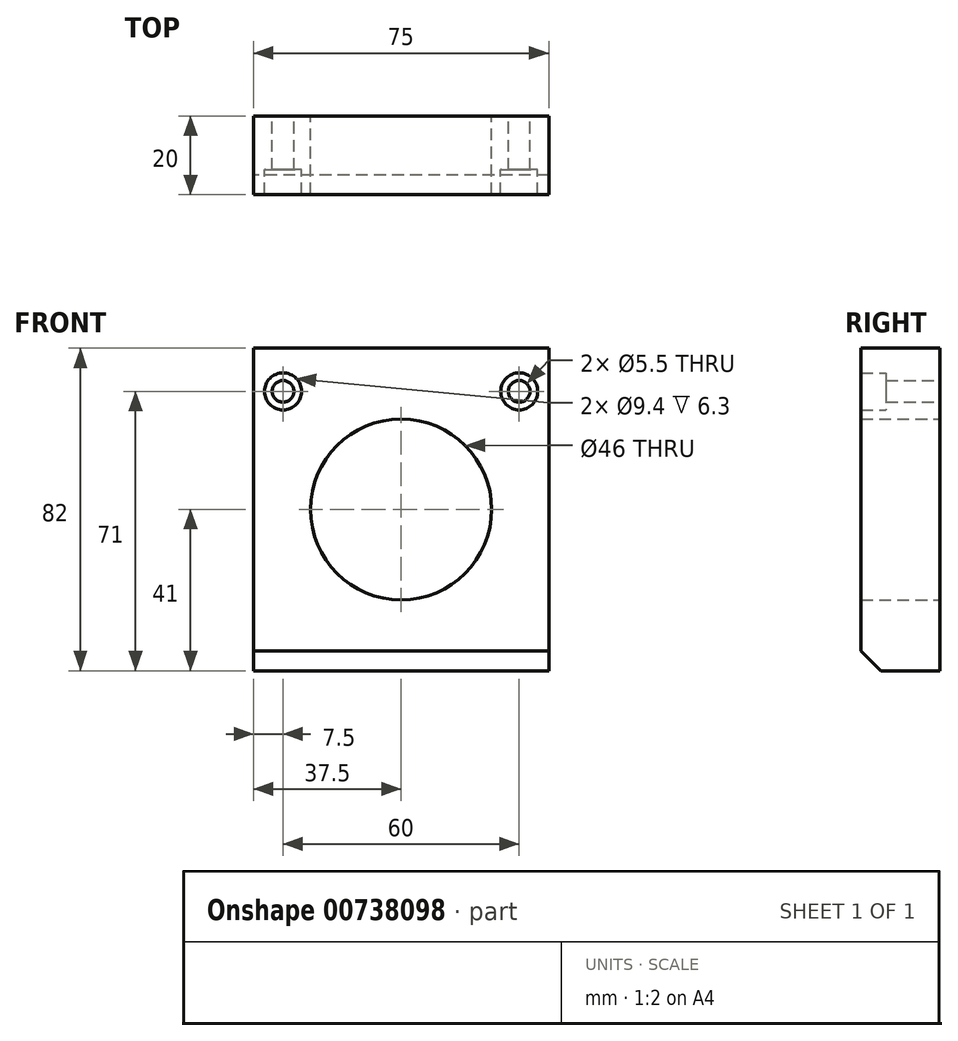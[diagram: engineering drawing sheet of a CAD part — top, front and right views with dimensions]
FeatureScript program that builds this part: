
annotation { "Feature Type Name" : "Feature", "Feature Type Description" : "" }
export const myFeature = defineFeature(function(context is Context, id is Id, definition is map)
    precondition{}
    {
        {
            var Q0;
            Q0=qCreatedBy(makeId("Front.planeOp"),FACE);
            var sketch = newSketch(context, id + "F0", { "sketchPlane" : qUnion([Q0])});
            skLineSegment(sketch, "E0.bottom", {"start": v(37.5, 41) * mm, "end": v(-37.5, 41) * mm});
            skLineSegment(sketch, "E0.top", {"start": v(37.5, -41) * mm, "end": v(-37.5, -41) * mm});
            skLineSegment(sketch, "E0.left", {"start": v(37.5, 41) * mm, "end": v(37.5, -41) * mm});
            skLineSegment(sketch, "E0.right", {"start": v(-37.5, 41) * mm, "end": v(-37.5, -41) * mm});
            skPoint(sketch, "E0.middle", {"position": v(0, 0) * mm});
            skSolve(sketch);
        }
        {
            var Q0;
            Q0=makeQuery(id+"F0.imprint","IMPRINT",FACE,{"disambiguationData":[TD([[makeQuery(id+"F0.imprint","IMPRINT",EDGE,{"derivedFrom":sQuery(id+"F0.wireOp",EDGE,"E0.bottom")}),1.0]])]});
            extrude(context, id + "F1", {"entities" : qUnion([Q0]), "depth" : 20 * mm, "offsetDistance" : 25 * mm});
        }
        {
            var Q0;
            Q0=makeQuery(id+"F1.opExtrude","CAP_FACE",FACE,{"disambiguationData":[OSD([sQuery(id+"F0.wireOp",EDGE,"E0.bottom"),sQuery(id+"F0.wireOp",EDGE,"E0.top"),sQuery(id+"F0.wireOp",EDGE,"E0.left"),sQuery(id+"F0.wireOp",EDGE,"E0.right")])],"isStart":false});
            var sketch = newSketch(context, id + "F2", { "sketchPlane" : qUnion([Q0])});
            skPoint(sketch, "E1", {"position": v(0, 0) * mm});
            skPoint(sketch, "E2", {"position": v(-30, 30) * mm});
            skPoint(sketch, "E3.MirrorP", {"position": v(30, 30) * mm});
            skSolve(sketch);
        }
        {
            var Q0;
            Q0=sQuery(id+"F2.wireOp",VERTEX,"E1");
            var Q1;
            Q1=makeQuery(id+"F1.opExtrude","SWEPT_BODY",BODY,{"disambiguationData":[OSD([sQuery(id+"F0.wireOp",EDGE,"E0.bottom"),sQuery(id+"F0.wireOp",EDGE,"E0.top"),sQuery(id+"F0.wireOp",EDGE,"E0.left"),sQuery(id+"F0.wireOp",EDGE,"E0.right")])]});
            hole(context, id + "F3", {"style" : HoleStyle.SIMPLE, "endStyle" : HoleEndStyle.THROUGH, "holeDiameter" : 46 * mm, "majorDiameter" : 5 * mm, "tappedDepth" : 12 * mm, "tapClearance" : 3, "startFromSketch" : true, "locations" : qUnion([Q0]), "scope" : qUnion([Q1])});
        }
        {
            var Q0;
            Q0=sQuery(id+"F2.wireOp",VERTEX,"E2");
            var Q1;
            Q1=sQuery(id+"F2.wireOp",VERTEX,"E3.MirrorP");
            var Q2;
            Q2=makeQuery(id+"F1.opExtrude","SWEPT_BODY",BODY,{"disambiguationData":[OSD([sQuery(id+"F0.wireOp",EDGE,"E0.bottom"),sQuery(id+"F0.wireOp",EDGE,"E0.top"),sQuery(id+"F0.wireOp",EDGE,"E0.left"),sQuery(id+"F0.wireOp",EDGE,"E0.right")])]});
            hole(context, id + "F4", {"style" : HoleStyle.C_BORE, "endStyle" : HoleEndStyle.THROUGH, "holeDiameter" : 5.5 * mm, "cBoreDiameter" : 9.4 * mm, "cBoreDepth" : 6.3 * mm, "majorDiameter" : 5 * mm, "tappedDepth" : 12 * mm, "tapClearance" : 3, "startFromSketch" : true, "locations" : qUnion([Q0, Q1]), "scope" : qUnion([Q2])});
        }
        {
            var Q0;
            Q0=makeQuery(id+"F1.opExtrude","CAP_EDGE",EDGE,{"disambiguationData":[OSD([sQuery(id+"F0.wireOp",EDGE,"E0.top")])],"isStart":false});
            chamfer(context, id + "F5", {"entities" : qUnion([Q0]), "width" : 5 * mm, "tangentPropagation" : true});
        }
    });
